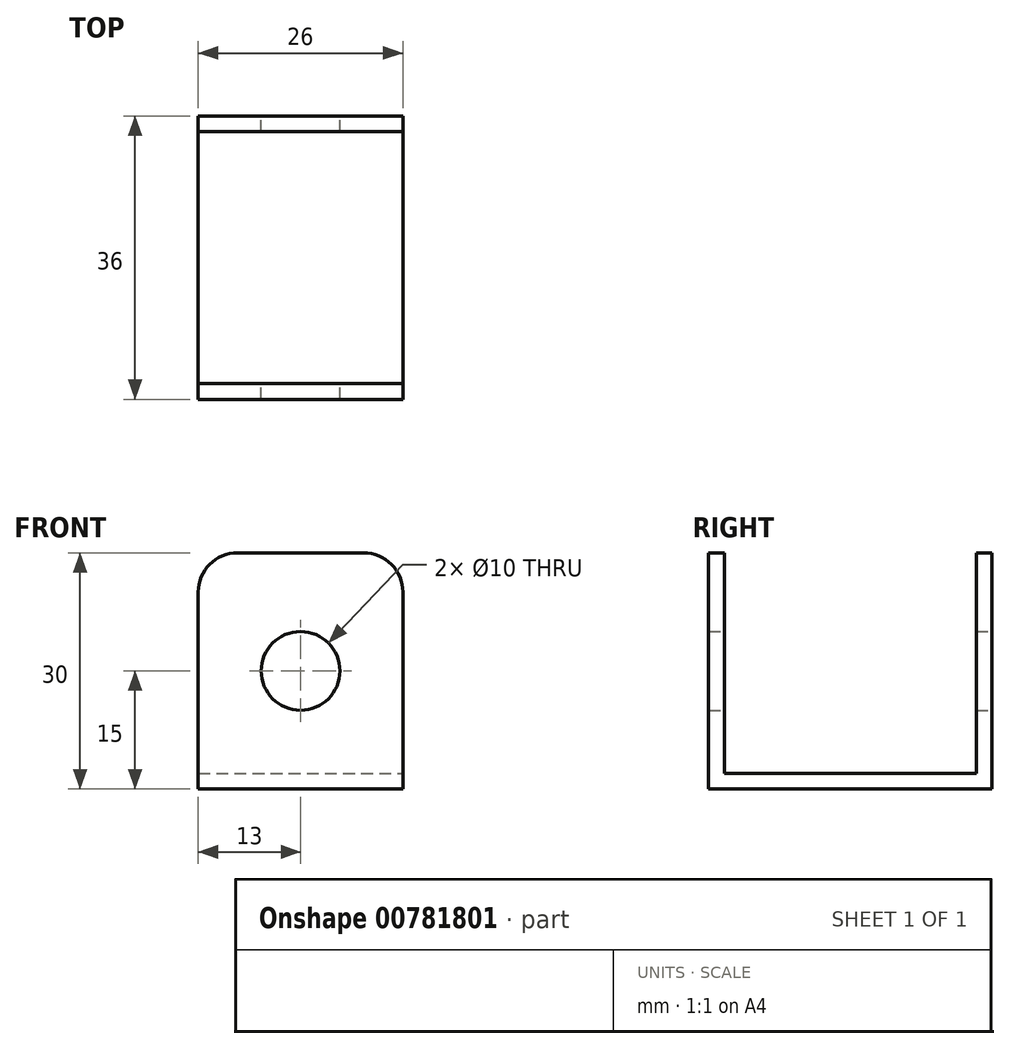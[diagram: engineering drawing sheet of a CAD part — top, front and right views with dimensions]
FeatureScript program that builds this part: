
annotation { "Feature Type Name" : "Feature", "Feature Type Description" : "" }
export const myFeature = defineFeature(function(context is Context, id is Id, definition is map)
    precondition{}
    {
        {
            var Q0;
            Q0=qCreatedBy(makeId("Top.planeOp"),FACE);
            var sketch = newSketch(context, id + "F0", { "sketchPlane" : qUnion([Q0])});
            skLineSegment(sketch, "E0.bottom", {"start": v(-13, 18) * mm, "end": v(13, 18) * mm});
            skLineSegment(sketch, "E0.top", {"start": v(-13, -18) * mm, "end": v(13, -18) * mm});
            skLineSegment(sketch, "E0.left", {"start": v(-13, 18) * mm, "end": v(-13, -18) * mm});
            skLineSegment(sketch, "E0.right", {"start": v(13, 18) * mm, "end": v(13, -18) * mm});
            skPoint(sketch, "E0.middle", {"position": v(0, 0) * mm});
            skLineSegment(sketch, "E1", {"start": v(-13, 16) * mm, "end": v(13, 16) * mm});
            skPoint(sketch, "E2.end.orphan", {"position": v(0, 16) * mm});
            skPoint(sketch, "E2.start.orphan", {"position": v(0, 18) * mm});
            skSolve(sketch);
        }
        {
            var Q0;
            {var subQ0=sQuery(id+"F0.wireOp",EDGE,"E0.bottom");Q0=makeQuery(id+"F0.imprint","IMPRINT",FACE,{"disambiguationData":[TD([[makeQuery(id+"F0.imprint","IMPRINT",EDGE,{"derivedFrom":subQ0}),-1.0]])]});}
            extrude(context, id + "F1", {"entities" : qUnion([Q0]), "depth" : 30 * mm, "offsetDistance" : 25 * mm});
        }
        {
            var Q0;
            {var subQ0=sQuery(id+"F0.wireOp",EDGE,"E0.top");Q0=makeQuery(id+"F0.imprint","IMPRINT",FACE,{"disambiguationData":[TD([[makeQuery(id+"F0.imprint","IMPRINT",EDGE,{"derivedFrom":subQ0}),1.0]])]});}
            extrude(context, id + "F2", {"entities" : qUnion([Q0]), "operationType" : NewBodyOperationType.ADD, "depth" : 2 * mm, "offsetDistance" : 25 * mm});
        }
        {
            var Q0;
            Q0=makeQuery(id+"F2.opExtrude","CAP_FACE",FACE,{"disambiguationData":[OSD([sQuery(id+"F0.wireOp",EDGE,"E0.top"),sQuery(id+"F0.wireOp",EDGE,"E0.left"),sQuery(id+"F0.wireOp",EDGE,"E0.right"),sQuery(id+"F0.wireOp",EDGE,"E1")])],"isStart":false});
            var sketch = newSketch(context, id + "F3", { "sketchPlane" : qUnion([Q0])});
            skLineSegment(sketch, "E3", {"start": v(0, -16) * mm, "end": v(13, -16) * mm});
            skLineSegment(sketch, "E4", {"start": v(13, -16) * mm, "end": v(-13, -16) * mm});
            skPoint(sketch, "E5.start.orphan", {"position": v(0, -18) * mm});
            skSolve(sketch);
        }
        {
            var Q0;
            Q0 = qSketchRegion(id + "F3", true);
            var Q1;
            {var subQ1=makeQuery(id+"F2.opExtrude","CAP_EDGE",EDGE,{"disambiguationData":[OSD([sQuery(id+"F0.wireOp",EDGE,"E0.top")])],"isStart":false});Q1=makeQuery(id+"F3.imprint","IMPRINT",FACE,{"disambiguationData":[TD([[makeQuery(id+"F3.imprint","IMPRINT",EDGE,{"derivedFrom":subQ1}),1.0]])]});}
            extrude(context, id + "F4", {"entities" : qUnion([Q0, Q1]), "operationType" : NewBodyOperationType.ADD, "depth" : 28 * mm, "offsetDistance" : 25 * mm});
        }
        {
            var Q0;
            Q0=makeQuery(id+"F4.opExtrude","CAP_EDGE",EDGE,{"disambiguationData":[OSD([sQuery(id+"F0.wireOp",EDGE,"E0.left")])],"isStart":false});
            fillet(context, id + "F5", {"entities" : qUnion([Q0]), "radius" : 5 * mm, "tangentPropagation" : true, "allowEdgeOverflow" : false});
        }
        {
            var Q0;
            Q0=makeQuery(id+"F1.opExtrude","CAP_EDGE",EDGE,{"disambiguationData":[OSD([sQuery(id+"F0.wireOp",EDGE,"E0.right")])],"isStart":false});
            var Q1;
            Q1=makeQuery(id+"F1.opExtrude","CAP_EDGE",EDGE,{"disambiguationData":[OSD([sQuery(id+"F0.wireOp",EDGE,"E0.left")])],"isStart":false});
            fillet(context, id + "F6", {"entities" : qUnion([Q0, Q1]), "radius" : 5 * mm, "tangentPropagation" : true, "allowEdgeOverflow" : false});
        }
        {
            var Q0;
            Q0=makeQuery(id+"F4.opExtrude","CAP_EDGE",EDGE,{"disambiguationData":[OSD([sQuery(id+"F0.wireOp",EDGE,"E0.right")])],"isStart":false});
            fillet(context, id + "F7", {"entities" : qUnion([Q0]), "radius" : 5 * mm, "tangentPropagation" : true, "allowEdgeOverflow" : false});
        }
        {
            var Q0;
            Q0=makeQuery(id+"F1.opExtrude","SWEPT_FACE",FACE,{"disambiguationData":[OSD([sQuery(id+"F0.wireOp",EDGE,"E0.bottom")])]});
            var sketch = newSketch(context, id + "F8", { "sketchPlane" : qUnion([Q0])});
            skLineSegment(sketch, "E6", {"start": v(0, 30) * mm, "end": v(0, 0) * mm});
            skCircle(sketch, "E7", {"center": v(0, 15) * mm, "radius": 5 * mm});
            skSolve(sketch);
        }
        {
            var Q0;
            Q0 = qSketchRegion(id + "F8", true);
            extrude(context, id + "F9", {"entities" : qUnion([Q0]), "operationType" : NewBodyOperationType.REMOVE, "oppositeDirection" : true, "depth" : 100 * mm, "offsetDistance" : 25 * mm});
        }
    });
